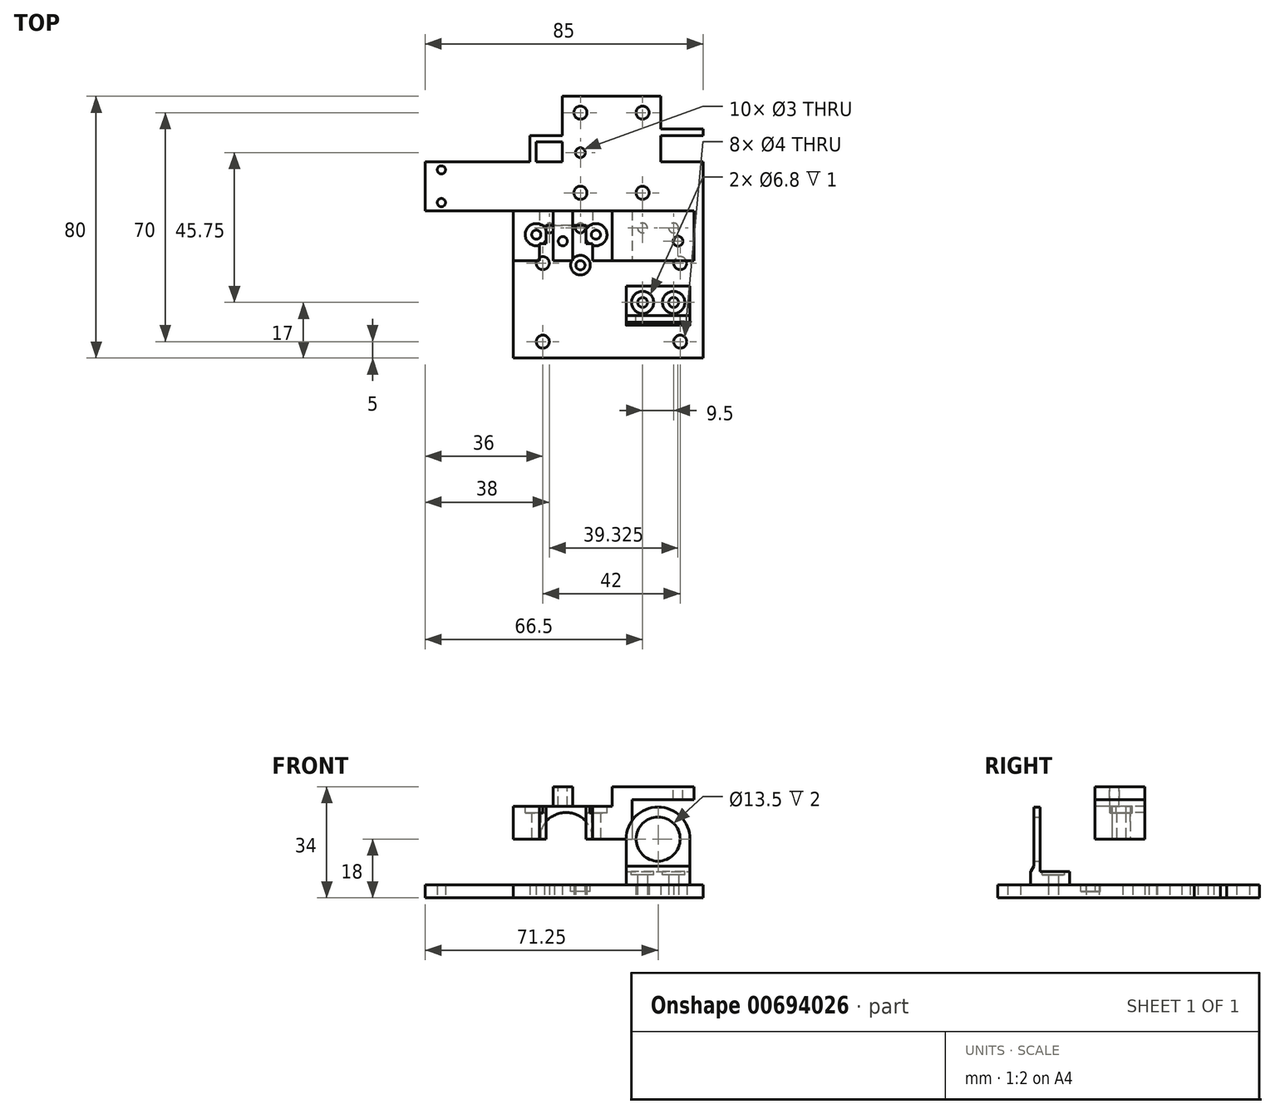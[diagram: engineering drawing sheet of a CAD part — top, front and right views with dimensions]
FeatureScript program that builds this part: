
annotation { "Feature Type Name" : "Feature", "Feature Type Description" : "" }
export const myFeature = defineFeature(function(context is Context, id is Id, definition is map)
    precondition{}
    {
        {
            var Q0;
            Q0=qCreatedBy(makeId("Top.planeOp"),FACE);
            var sketch = newSketch(context, id + "F0", { "sketchPlane" : qUnion([Q0])});
            skLineSegment(sketch, "E0.bottom", {"start": v(0, 0) * mm, "end": v(58, 0) * mm});
            skLineSegment(sketch, "E0.top", {"start": v(0, -60) * mm, "end": v(58, -60) * mm});
            skLineSegment(sketch, "E0.left", {"start": v(0, 0) * mm, "end": v(0, -60) * mm});
            skLineSegment(sketch, "E0.right", {"start": v(58, 0) * mm, "end": v(58, -60) * mm});
            skLineSegment(sketch, "E1.bottom", {"start": v(15, 0) * mm, "end": v(45, 0) * mm});
            skLineSegment(sketch, "E1.top", {"start": v(15, 20) * mm, "end": v(45, 20) * mm});
            skLineSegment(sketch, "E1.left", {"start": v(15, 0) * mm, "end": v(15, 20) * mm});
            skLineSegment(sketch, "E1.right", {"start": v(45, 0) * mm, "end": v(45, 20) * mm});
            skLineSegment(sketch, "E2.bottom", {"start": v(0, 0) * mm, "end": v(-27, 0) * mm});
            skLineSegment(sketch, "E2.top", {"start": v(0, -15) * mm, "end": v(-27, -15) * mm});
            skLineSegment(sketch, "E2.left", {"start": v(0, 0) * mm, "end": v(0, -15) * mm});
            skLineSegment(sketch, "E2.right", {"start": v(-27, 0) * mm, "end": v(-27, -15) * mm});
            skCircle(sketch, "E3", {"center": v(20.5, 15) * mm, "radius": 2 * mm});
            skLineSegment(sketch, "E4", {"start": v(30, 20) * mm, "end": v(30, -60) * mm, "construction": true});
            skCircle(sketch, "E5.MirrorC", {"center": v(39.5, 15) * mm, "radius": 2 * mm});
            skCircle(sketch, "E6", {"center": v(20.5, -9.5) * mm, "radius": 2 * mm});
            skCircle(sketch, "E7.MirrorC", {"center": v(39.5, -9.5) * mm, "radius": 2 * mm});
            skCircle(sketch, "E8", {"center": v(51, -55) * mm, "radius": 2 * mm});
            skCircle(sketch, "E9.MirrorC", {"center": v(9, -55) * mm, "radius": 2 * mm});
            skCircle(sketch, "E10", {"center": v(51, -31) * mm, "radius": 2 * mm});
            skCircle(sketch, "E11.MirrorC", {"center": v(9, -31) * mm, "radius": 2 * mm});
            skCircle(sketch, "E12", {"center": v(-22, -2.5) * mm, "radius": 1.25 * mm});
            skLineSegment(sketch, "E13", {"start": v(-27, -7.5) * mm, "end": v(0, -7.5) * mm, "construction": true});
            skCircle(sketch, "E14.MirrorC", {"center": v(-22, -12.5) * mm, "radius": 1.25 * mm});
            skLineSegment(sketch, "E15", {"start": v(20.5, -9.5) * mm, "end": v(20.5, -31) * mm, "construction": true});
            skCircle(sketch, "E16", {"center": v(20.5, -20.25) * mm, "radius": 1.5 * mm});
            skCircle(sketch, "E17", {"center": v(11, -20.25) * mm, "radius": 1.5 * mm});
            skCircle(sketch, "E18.MirrorC", {"center": v(39.5, -20.25) * mm, "radius": 1.5 * mm});
            skCircle(sketch, "E19.MirrorC", {"center": v(49, -20.25) * mm, "radius": 1.5 * mm});
            skCircle(sketch, "E20", {"center": v(30, -20.25) * mm, "radius": 1.5 * mm});
            skPoint(sketch, "E20.centerSnap0", {"position": v(30, -20) * mm});
            skLineSegment(sketch, "E21", {"start": v(9, -31) * mm, "end": v(9, -55) * mm, "construction": true});
            skLineSegment(sketch, "E22", {"start": v(9, -43) * mm, "end": v(58, -43) * mm, "construction": true});
            skLineSegment(sketch, "E23", {"start": v(39.5, -20.25) * mm, "end": v(39.5, -43) * mm, "construction": true});
            skLineSegment(sketch, "E24", {"start": v(39.5, -31.63) * mm, "end": v(0, -31.63) * mm, "construction": true});
            skCircle(sketch, "E25.MirrorC", {"center": v(49, -43) * mm, "radius": 1.5 * mm});
            skCircle(sketch, "E26.MirrorC", {"center": v(39.5, -43) * mm, "radius": 1.5 * mm});
            skCircle(sketch, "E27", {"center": v(30, -31.63) * mm, "radius": 1.5 * mm});
            skCircle(sketch, "E28", {"center": v(39.5, -31.63) * mm, "radius": 1.5 * mm});
            skCircle(sketch, "E29", {"center": v(20.5, -31.63) * mm, "radius": 1.5 * mm});
            skLineSegment(sketch, "E30", {"start": v(39.5, 15) * mm, "end": v(39.5, -9.5) * mm, "construction": true});
            skCircle(sketch, "E31", {"center": v(39.5, 2.75) * mm, "radius": 1.5 * mm});
            skCircle(sketch, "E32.MirrorC", {"center": v(20.5, 2.75) * mm, "radius": 1.5 * mm});
            skCircle(sketch, "E33", {"center": v(30, 2.75) * mm, "radius": 1.5 * mm});
            skLineSegment(sketch, "E34.bottom", {"start": v(58, 0) * mm, "end": v(45, 0) * mm});
            skLineSegment(sketch, "E34.top", {"start": v(58, 8) * mm, "end": v(45, 8) * mm});
            skLineSegment(sketch, "E34.left", {"start": v(58, 0) * mm, "end": v(58, 8) * mm});
            skLineSegment(sketch, "E34.right", {"start": v(45, 0) * mm, "end": v(45, 8) * mm});
            skLineSegment(sketch, "E35.top", {"start": v(58, 10) * mm, "end": v(45, 10) * mm});
            skLineSegment(sketch, "E35.left", {"start": v(58, 8) * mm, "end": v(58, 10) * mm});
            skLineSegment(sketch, "E35.right", {"start": v(45, 8) * mm, "end": v(45, 10) * mm});
            skLineSegment(sketch, "E36.bottom", {"start": v(58, 8) * mm, "end": v(56, 8) * mm});
            skLineSegment(sketch, "E36.top", {"start": v(58, 0) * mm, "end": v(56, 0) * mm});
            skLineSegment(sketch, "E36.left", {"start": v(58, 8) * mm, "end": v(58, 0) * mm});
            skLineSegment(sketch, "E36.right", {"start": v(56, 8) * mm, "end": v(56, 0) * mm});
            skLineSegment(sketch, "E37.bottom", {"start": v(15, 0) * mm, "end": v(7, 0) * mm});
            skLineSegment(sketch, "E37.top", {"start": v(15, 6) * mm, "end": v(7, 6) * mm});
            skLineSegment(sketch, "E37.left", {"start": v(15, 0) * mm, "end": v(15, 6) * mm});
            skLineSegment(sketch, "E37.right", {"start": v(7, 0) * mm, "end": v(7, 6) * mm});
            skLineSegment(sketch, "E38.0", {"start": v(5, 0) * mm, "end": v(5, 8) * mm});
            skLineSegment(sketch, "E38.1", {"start": v(15, 8) * mm, "end": v(5, 8) * mm});
            skSolve(sketch);
        }
        {
            var Q0;
            Q0=makeQuery(id+"F0.imprint","IMPRINT",FACE,{"disambiguationData":[TD([[makeQuery(id+"F0.imprint","IMPRINT",EDGE,{"derivedFrom":sQuery(id+"F0.wireOp",EDGE,"E0.top")}),1.0]])]});
            var Q1;
            Q1=makeQuery(id+"F0.imprint","IMPRINT",FACE,{"disambiguationData":[TD([[makeQuery(id+"F0.imprint","IMPRINT",EDGE,{"derivedFrom":sQuery(id+"F0.wireOp",EDGE,"E2.bottom")}),1.0]])]});
            var Q2;
            Q2=makeQuery(id+"F0.imprint","IMPRINT",FACE,{"disambiguationData":[TD([[makeQuery(id+"F0.imprint","IMPRINT",EDGE,{"derivedFrom":sQuery(id+"F0.wireOp",EDGE,"E1.bottom")}),1.0]])]});
            var Q3;
            Q3=makeQuery(id+"F0.imprint","IMPRINT",FACE,{"disambiguationData":[TD([[makeQuery(id+"F0.imprint","IMPRINT",EDGE,{"derivedFrom":sQuery(id+"F0.wireOp",EDGE,"E20")}),1.0]])]});
            var Q4;
            Q4=makeQuery(id+"F0.imprint","IMPRINT",FACE,{"disambiguationData":[TD([[makeQuery(id+"F0.imprint","IMPRINT",EDGE,{"derivedFrom":sQuery(id+"F0.wireOp",EDGE,"E18.MirrorC")}),-1.0]])]});
            var Q5;
            Q5=makeQuery(id+"F0.imprint","IMPRINT",FACE,{"disambiguationData":[TD([[makeQuery(id+"F0.imprint","IMPRINT",EDGE,{"derivedFrom":sQuery(id+"F0.wireOp",EDGE,"E19.MirrorC")}),-1.0]])]});
            var Q6;
            Q6=makeQuery(id+"F0.imprint","IMPRINT",FACE,{"disambiguationData":[TD([[makeQuery(id+"F0.imprint","IMPRINT",EDGE,{"derivedFrom":sQuery(id+"F0.wireOp",EDGE,"E27")}),1.0]])]});
            var Q7;
            Q7=makeQuery(id+"F0.imprint","IMPRINT",FACE,{"disambiguationData":[TD([[makeQuery(id+"F0.imprint","IMPRINT",EDGE,{"derivedFrom":sQuery(id+"F0.wireOp",EDGE,"E28")}),1.0]])]});
            var Q8;
            Q8=makeQuery(id+"F0.imprint","IMPRINT",FACE,{"disambiguationData":[TD([[makeQuery(id+"F0.imprint","IMPRINT",EDGE,{"derivedFrom":sQuery(id+"F0.wireOp",EDGE,"E32.MirrorC")}),-1.0]])]});
            var Q9;
            Q9=makeQuery(id+"F0.imprint","IMPRINT",FACE,{"disambiguationData":[TD([[makeQuery(id+"F0.imprint","IMPRINT",EDGE,{"derivedFrom":sQuery(id+"F0.wireOp",EDGE,"E33")}),1.0]])]});
            var Q10;
            Q10=makeQuery(id+"F0.imprint","IMPRINT",FACE,{"disambiguationData":[TD([[makeQuery(id+"F0.imprint","IMPRINT",EDGE,{"derivedFrom":sQuery(id+"F0.wireOp",EDGE,"E31")}),1.0]])]});
            var Q11;
            Q11=makeQuery(id+"F0.imprint","IMPRINT",FACE,{"disambiguationData":[TD([[makeQuery(id+"F0.imprint","IMPRINT",EDGE,{"derivedFrom":sQuery(id+"F0.wireOp",EDGE,"E29")}),1.0]])]});
            var Q12;
            Q12=makeQuery(id+"F0.imprint","IMPRINT",FACE,{"disambiguationData":[TD([[makeQuery(id+"F0.imprint","IMPRINT",EDGE,{"derivedFrom":sQuery(id+"F0.wireOp",EDGE,"E34.top")}),-1.0]])]});
            var Q13;
            Q13=makeQuery(id+"F0.imprint","IMPRINT",FACE,{"disambiguationData":[TD([[makeQuery(id+"F0.imprint","IMPRINT",EDGE,{"derivedFrom":sQuery(id+"F0.wireOp",EDGE,"E36.bottom")}),1.0]])]});
            var Q14;
            {var subQ0=sQuery(id+"F0.wireOp",EDGE,"XzGVJkhi-AcDU-f53J-RqIE-YCnuyh9zdkUA");Q14=makeQuery(id+"F0.imprint","IMPRINT",FACE,{"disambiguationData":[TD([[makeQuery(id+"F0.imprint","IMPRINT",EDGE,{"derivedFrom":subQ0}),-1.0]])]});}
            var Q15;
            Q15 = qSketchRegion(id + "F2", true);
            var Q16;
            {var subQ0=sQuery(id+"F0.wireOp",EDGE,"E37.top");Q16=makeQuery(id+"F0.imprint","IMPRINT",FACE,{"disambiguationData":[TD([[makeQuery(id+"F0.imprint","IMPRINT",EDGE,{"derivedFrom":subQ0}),-1.0]])]});}
            extrude(context, id + "F1", {"entities" : qUnion([Q0, Q1, Q2, Q3, Q4, Q5, Q6, Q7, Q8, Q9, Q10, Q11, Q12, Q13, Q14, Q15, Q16]), "depth" : 4 * mm, "offsetDistance" : 25 * mm});
        }
        {
            var Q0;
            Q0=makeQuery(id+"F1.opExtrude","CAP_FACE",FACE,{"disambiguationData":[OSD([sQuery(id+"F0.wireOp",EDGE,"E0.bottom"),sQuery(id+"F0.wireOp",EDGE,"E0.top"),sQuery(id+"F0.wireOp",EDGE,"E0.left"),sQuery(id+"F0.wireOp",EDGE,"E0.right"),sQuery(id+"F0.wireOp",EDGE,"E1.top"),sQuery(id+"F0.wireOp",EDGE,"E1.left"),sQuery(id+"F0.wireOp",EDGE,"E1.right"),sQuery(id+"F0.wireOp",EDGE,"E2.bottom"),sQuery(id+"F0.wireOp",EDGE,"E2.top"),sQuery(id+"F0.wireOp",EDGE,"E2.right"),sQuery(id+"F0.wireOp",EDGE,"E3"),sQuery(id+"F0.wireOp",EDGE,"E5.MirrorC"),sQuery(id+"F0.wireOp",EDGE,"E6"),sQuery(id+"F0.wireOp",EDGE,"E7.MirrorC"),sQuery(id+"F0.wireOp",EDGE,"E8"),sQuery(id+"F0.wireOp",EDGE,"E9.MirrorC"),sQuery(id+"F0.wireOp",EDGE,"E10"),sQuery(id+"F0.wireOp",EDGE,"E11.MirrorC"),sQuery(id+"F0.wireOp",EDGE,"E12"),sQuery(id+"F0.wireOp",EDGE,"E14.MirrorC"),sQuery(id+"F0.wireOp",EDGE,"E16"),sQuery(id+"F0.wireOp",EDGE,"E17"),sQuery(id+"F0.wireOp",EDGE,"E18.MirrorC"),sQuery(id+"F0.wireOp",EDGE,"E19.MirrorC"),sQuery(id+"F0.wireOp",EDGE,"E20"),sQuery(id+"F0.wireOp",EDGE,"E25.MirrorC"),sQuery(id+"F0.wireOp",EDGE,"E26.MirrorC"),sQuery(id+"F0.wireOp",EDGE,"a45dcdff-8f47-47a6-94de-daccb21566b90.MirrorC"),sQuery(id+"F0.wireOp",EDGE,"c506a873-8e33-4dee-948d-999e04e901bd0.MirrorC"),sQuery(id+"F0.wireOp",EDGE,"0d328794-d52e-4739-910c-511e7e9b0b190.MirrorC"),sQuery(id+"F0.wireOp",EDGE,"E27"),sQuery(id+"F0.wireOp",EDGE,"E28"),sQuery(id+"F0.wireOp",EDGE,"E29"),sQuery(id+"F0.wireOp",EDGE,"E31"),sQuery(id+"F0.wireOp",EDGE,"E32.MirrorC"),sQuery(id+"F0.wireOp",EDGE,"E33")])],"isStart":false});
            var sketch = newSketch(context, id + "F2", { "sketchPlane" : qUnion([Q0])});
            skLineSegment(sketch, "E39.0", {"start": v(0, -15) * mm, "end": v(0, -60) * mm});
            skLineSegment(sketch, "E39.1", {"start": v(-27, 0) * mm, "end": v(5, 0) * mm});
            skLineSegment(sketch, "E39.2", {"start": v(0, -15) * mm, "end": v(-27, -15) * mm});
            skLineSegment(sketch, "E39.3", {"start": v(0, -60) * mm, "end": v(58, -60) * mm});
            skLineSegment(sketch, "E39.4", {"start": v(58, -60) * mm, "end": v(58, -60) * mm});
            skLineSegment(sketch, "E39.5", {"start": v(5, 0) * mm, "end": v(58, 0) * mm});
            skLineSegment(sketch, "E39.6", {"start": v(45, 0) * mm, "end": v(45, 20) * mm});
            skLineSegment(sketch, "E39.7", {"start": v(15, 0) * mm, "end": v(15, 20) * mm});
            skLineSegment(sketch, "E39.8", {"start": v(15, 20) * mm, "end": v(45, 20) * mm});
            skCircle(sketch, "E39.9", {"center": v(11, -20.25) * mm, "radius": 1.5 * mm});
            skCircle(sketch, "E39.10", {"center": v(20.5, -20.25) * mm, "radius": 1.5 * mm});
            skCircle(sketch, "E39.11", {"center": v(20.5, -31.63) * mm, "radius": 1.4 * mm});
            skCircle(sketch, "E40.0", {"center": v(9, -31) * mm, "radius": 2 * mm});
            skLineSegment(sketch, "E41", {"start": v(7, 0) * mm, "end": v(7, -60) * mm, "construction": true});
            skCircle(sketch, "E42.0", {"center": v(20.5, -9.5) * mm, "radius": 2 * mm});
            skLineSegment(sketch, "E43", {"start": v(20.5, -9.5) * mm, "end": v(20.5, -20.25) * mm, "construction": true});
            skPoint(sketch, "E44", {"position": v(20.5, -14.88) * mm});
            skLineSegment(sketch, "E45", {"start": v(7, -15) * mm, "end": v(25.25, -15) * mm});
            skLineSegment(sketch, "E46", {"start": v(7, -37.31) * mm, "end": v(25.25, -37.31) * mm});
            skLineSegment(sketch, "E47", {"start": v(25.25, -37.31) * mm, "end": v(25.25, -15) * mm});
            skCircle(sketch, "E48", {"center": v(9, -31) * mm, "radius": 6.31 * mm});
            skLineSegment(sketch, "E49", {"start": v(9, -24.69) * mm, "end": v(7, -24.69) * mm});
            skLineSegment(sketch, "E50", {"start": v(15.31, -31) * mm, "end": v(15.31, -37.31) * mm});
            skLineSegment(sketch, "E51", {"start": v(7, -15) * mm, "end": v(7, -24.69) * mm});
            skSolve(sketch);
        }
        {
            var Q0;
            Q0=makeQuery(id+"F2.imprint","IMPRINT",FACE,{"disambiguationData":[TD([[makeQuery(id+"F2.imprint","IMPRINT",EDGE,{"derivedFrom":sQuery(id+"F2.wireOp",EDGE,"E39.9")}),-1.0]])]});
            extrude(context, id + "F3", {"entities" : qUnion([Q0]), "depth" : 4 * mm, "offsetDistance" : 25 * mm});
        }
        {
            var Q0;
            Q0=makeQuery(id+"F1.opExtrude","CAP_FACE",FACE,{"disambiguationData":[OSD([sQuery(id+"F0.wireOp",EDGE,"E0.bottom"),sQuery(id+"F0.wireOp",EDGE,"E0.top"),sQuery(id+"F0.wireOp",EDGE,"E0.left"),sQuery(id+"F0.wireOp",EDGE,"E0.right"),sQuery(id+"F0.wireOp",EDGE,"E1.top"),sQuery(id+"F0.wireOp",EDGE,"E1.left"),sQuery(id+"F0.wireOp",EDGE,"E1.right"),sQuery(id+"F0.wireOp",EDGE,"E2.bottom"),sQuery(id+"F0.wireOp",EDGE,"E2.top"),sQuery(id+"F0.wireOp",EDGE,"E2.right"),sQuery(id+"F0.wireOp",EDGE,"E3"),sQuery(id+"F0.wireOp",EDGE,"E5.MirrorC"),sQuery(id+"F0.wireOp",EDGE,"E6"),sQuery(id+"F0.wireOp",EDGE,"E7.MirrorC"),sQuery(id+"F0.wireOp",EDGE,"E8"),sQuery(id+"F0.wireOp",EDGE,"E9.MirrorC"),sQuery(id+"F0.wireOp",EDGE,"E10"),sQuery(id+"F0.wireOp",EDGE,"E11.MirrorC"),sQuery(id+"F0.wireOp",EDGE,"E12"),sQuery(id+"F0.wireOp",EDGE,"E14.MirrorC"),sQuery(id+"F0.wireOp",EDGE,"E16"),sQuery(id+"F0.wireOp",EDGE,"E17"),sQuery(id+"F0.wireOp",EDGE,"E25.MirrorC"),sQuery(id+"F0.wireOp",EDGE,"E26.MirrorC")])],"isStart":false});
            var sketch = newSketch(context, id + "F4", { "sketchPlane" : qUnion([Q0])});
            skCircle(sketch, "E52.0", {"center": v(11, -20.25) * mm, "radius": 1.5 * mm});
            skCircle(sketch, "E52.1", {"center": v(20.5, -20.25) * mm, "radius": 1.5 * mm});
            skCircle(sketch, "E52.2", {"center": v(20.5, -31.63) * mm, "radius": 1.4 * mm});
            skCircle(sketch, "E53", {"center": v(20.5, -31.63) * mm, "radius": 3 * mm});
            skLineSegment(sketch, "E54.0", {"start": v(7, -15) * mm, "end": v(25.25, -15) * mm});
            skLineSegment(sketch, "E54.1", {"start": v(7, -15) * mm, "end": v(7, -24.69) * mm});
            skLineSegment(sketch, "E54.4", {"start": v(25.25, -37.31) * mm, "end": v(25.25, -15) * mm});
            skLineSegment(sketch, "E54.5", {"start": v(9, -24.69) * mm, "end": v(7, -24.69) * mm});
            skArc(sketch, "E54.6", {"start": v(15.31, -31) * mm, "mid": v(13.46, -26.54) * mm, "end": v(9, -24.69) * mm});
            skLineSegment(sketch, "E54.7", {"start": v(15.31, -31) * mm, "end": v(15.31, -37.31) * mm});
            skLineSegment(sketch, "E54.8", {"start": v(15.31, -37.31) * mm, "end": v(25.25, -37.31) * mm});
            skLineSegment(sketch, "E55", {"start": v(9, -24.69) * mm, "end": v(25.25, -24.69) * mm});
            skSolve(sketch);
        }
        {
            var Q0;
            Q0=makeQuery(id+"F4.imprint","IMPRINT",FACE,{"disambiguationData":[TD([[makeQuery(id+"F4.imprint","IMPRINT",EDGE,{"derivedFrom":sQuery(id+"F4.wireOp",EDGE,"E52.2")}),-1.0]])]});
            extrude(context, id + "F5", {"entities" : qUnion([Q0]), "operationType" : NewBodyOperationType.REMOVE, "oppositeDirection" : true, "depth" : 2 * mm, "offsetDistance" : 25 * mm});
        }
        {
            var Q0;
            Q0=makeQuery(id+"F4.imprint","IMPRINT",FACE,{"disambiguationData":[TD([[makeQuery(id+"F4.imprint","IMPRINT",EDGE,{"derivedFrom":sQuery(id+"F4.wireOp",EDGE,"E52.0")}),-1.0]])]});
            extrude(context, id + "F6", {"entities" : qUnion([Q0]), "depth" : 4 * mm, "offsetDistance" : 25 * mm});
        }
        {
            var Q0;
            Q0=makeQuery(id+"F6.opExtrude","CAP_FACE",FACE,{"disambiguationData":[OSD([sQuery(id+"F4.wireOp",EDGE,"E52.0"),sQuery(id+"F4.wireOp",EDGE,"E52.1"),sQuery(id+"F4.wireOp",EDGE,"E54.0"),sQuery(id+"F4.wireOp",EDGE,"E54.1"),sQuery(id+"F4.wireOp",EDGE,"E54.4"),sQuery(id+"F4.wireOp",EDGE,"E54.5"),sQuery(id+"F4.wireOp",EDGE,"E55")])],"isStart":false});
            var sketch = newSketch(context, id + "F7", { "sketchPlane" : qUnion([Q0])});
            skLineSegment(sketch, "E56.0", {"start": v(7, -15) * mm, "end": v(7, -24.69) * mm});
            skLineSegment(sketch, "E56.1", {"start": v(7, -15) * mm, "end": v(25.25, -15) * mm});
            skLineSegment(sketch, "E56.2", {"start": v(25.25, -24.69) * mm, "end": v(7, -24.69) * mm});
            skLineSegment(sketch, "E56.3", {"start": v(25.25, -24.69) * mm, "end": v(25.25, -15) * mm});
            skLineSegment(sketch, "E57.0", {"start": v(15.31, -31) * mm, "end": v(15.31, -37.31) * mm});
            skLineSegment(sketch, "E57.1", {"start": v(15.31, -37.31) * mm, "end": v(25.25, -37.31) * mm});
            skLineSegment(sketch, "E57.2", {"start": v(25.25, -37.31) * mm, "end": v(25.25, -15) * mm});
            skArc(sketch, "E57.3", {"start": v(15.31, -31) * mm, "mid": v(13.46, -26.54) * mm, "end": v(9, -24.69) * mm});
            skLineSegment(sketch, "E58", {"start": v(7, -24.69) * mm, "end": v(7, -37.31) * mm});
            skLineSegment(sketch, "E59", {"start": v(7, -37.31) * mm, "end": v(15.31, -37.31) * mm});
            skLineSegment(sketch, "E60.bottom", {"start": v(7, -15) * mm, "end": v(4, -15) * mm});
            skLineSegment(sketch, "E60.top", {"start": v(7, -37.31) * mm, "end": v(4, -37.31) * mm});
            skLineSegment(sketch, "E60.left", {"start": v(7, -15) * mm, "end": v(7, -37.31) * mm});
            skLineSegment(sketch, "E60.right", {"start": v(4, -15) * mm, "end": v(4, -37.31) * mm});
            skLineSegment(sketch, "E61.bottom", {"start": v(25.25, -15) * mm, "end": v(28.25, -15) * mm});
            skLineSegment(sketch, "E61.top", {"start": v(25.25, -37.31) * mm, "end": v(28.25, -37.31) * mm});
            skLineSegment(sketch, "E61.left", {"start": v(25.25, -15) * mm, "end": v(25.25, -37.31) * mm});
            skLineSegment(sketch, "E61.right", {"start": v(28.25, -15) * mm, "end": v(28.25, -37.31) * mm});
            skSolve(sketch);
        }
        {
            var Q0;
            {var subQ1=sQuery(id+"F7.wireOp",EDGE,"E56.1");Q0=makeQuery(id+"F7.imprint","IMPRINT",FACE,{"disambiguationData":[TD([[makeQuery(id+"F7.imprint","IMPRINT",EDGE,{"derivedFrom":subQ1}),-1.0]])]});}
            var Q1;
            {var subQ3=sQuery(id+"F7.wireOp",EDGE,"E60.bottom");Q1=makeQuery(id+"F7.imprint","IMPRINT",FACE,{"disambiguationData":[TD([[makeQuery(id+"F7.imprint","IMPRINT",EDGE,{"derivedFrom":subQ3}),1.0]])]});}
            var Q2;
            Q2=makeQuery(id+"F7.imprint","IMPRINT",FACE,{"disambiguationData":[TD([[makeQuery(id+"F7.imprint","IMPRINT",EDGE,{"derivedFrom":sQuery(id+"F7.wireOp",EDGE,"E57.0")}),-1.0]])]});
            var Q3;
            Q3=makeQuery(id+"F7.imprint","IMPRINT",FACE,{"disambiguationData":[TD([[makeQuery(id+"F7.imprint","IMPRINT",EDGE,{"derivedFrom":sQuery(id+"F7.wireOp",EDGE,"E57.0")}),1.0]])]});
            var Q4;
            {var subQ1=sQuery(id+"F7.wireOp",EDGE,"E61.bottom");Q4=makeQuery(id+"F7.imprint","IMPRINT",FACE,{"disambiguationData":[TD([[makeQuery(id+"F7.imprint","IMPRINT",EDGE,{"derivedFrom":subQ1}),-1.0]])]});}
            var Q5;
            Q5=makeQuery(id+"F7.imprint","IMPRINT",FACE,{"disambiguationData":[TD([[makeQuery(id+"F7.imprint","IMPRINT",EDGE,{"derivedFrom":makeQuery(id+"F6.opExtrude","CAP_EDGE",EDGE,{"disambiguationData":[OSD([sQuery(id+"F4.wireOp",EDGE,"E52.0")])],"isStart":false})}),1.0]])]});
            var Q6;
            Q6=makeQuery(id+"F7.imprint","IMPRINT",FACE,{"disambiguationData":[TD([[makeQuery(id+"F7.imprint","IMPRINT",EDGE,{"derivedFrom":makeQuery(id+"F6.opExtrude","CAP_EDGE",EDGE,{"disambiguationData":[OSD([sQuery(id+"F4.wireOp",EDGE,"E52.1")])],"isStart":false})}),1.0]])]});
            extrude(context, id + "F8", {"entities" : qUnion([Q0, Q1, Q2, Q3, Q4, Q5, Q6]), "operationType" : NewBodyOperationType.ADD, "depth" : 10 * mm, "offsetDistance" : 25 * mm});
        }
        {
            var Q0;
            Q0=makeQuery(id+"F8.opExtrude","CAP_FACE",FACE,{"disambiguationData":[OSD([sQuery(id+"F7.wireOp",EDGE,"E56.0"),sQuery(id+"F7.wireOp",EDGE,"E56.1"),sQuery(id+"F7.wireOp",EDGE,"E57.1"),sQuery(id+"F7.wireOp",EDGE,"E57.2"),sQuery(id+"F7.wireOp",EDGE,"E58"),sQuery(id+"F7.wireOp",EDGE,"E59")])],"isStart":false});
            var sketch = newSketch(context, id + "F9", { "sketchPlane" : qUnion([Q0])});
            skLineSegment(sketch, "E62", {"start": v(16.13, -15) * mm, "end": v(16.13, -37.31) * mm, "construction": true});
            skLineSegment(sketch, "E63.bottom", {"start": v(16.13, -15) * mm, "end": v(24.23, -15) * mm});
            skLineSegment(sketch, "E63.top", {"start": v(16.13, -19.5) * mm, "end": v(24.23, -19.5) * mm});
            skLineSegment(sketch, "E63.left", {"start": v(16.13, -15) * mm, "end": v(16.13, -19.5) * mm});
            skLineSegment(sketch, "E63.right", {"start": v(24.23, -15) * mm, "end": v(24.23, -19.5) * mm});
            skLineSegment(sketch, "E64.bottom", {"start": v(16.13, -19.5) * mm, "end": v(22.23, -19.5) * mm});
            skLineSegment(sketch, "E64.top", {"start": v(16.13, -25.1) * mm, "end": v(22.23, -25.1) * mm});
            skLineSegment(sketch, "E64.left", {"start": v(16.13, -19.5) * mm, "end": v(16.13, -25.1) * mm});
            skLineSegment(sketch, "E64.right", {"start": v(22.23, -19.5) * mm, "end": v(22.23, -25.1) * mm});
            skLineSegment(sketch, "E65.bottom", {"start": v(16.13, -25.1) * mm, "end": v(24.23, -25.1) * mm});
            skLineSegment(sketch, "E65.top", {"start": v(16.13, -30.3) * mm, "end": v(24.23, -30.3) * mm});
            skLineSegment(sketch, "E65.left", {"start": v(16.13, -25.1) * mm, "end": v(16.13, -30.3) * mm});
            skLineSegment(sketch, "E65.right", {"start": v(24.23, -25.1) * mm, "end": v(24.23, -30.3) * mm});
            skLineSegment(sketch, "E66.left", {"start": v(16.13, -30.3) * mm, "end": v(16.13, -37.31) * mm});
            skLineSegment(sketch, "E67", {"start": v(22.23, -22.3) * mm, "end": v(28.25, -22.3) * mm, "construction": true});
            skCircle(sketch, "E68", {"center": v(25.24, -22.3) * mm, "radius": 1.4 * mm});
            skCircle(sketch, "E69.MirrorC", {"center": v(7.01, -22.3) * mm, "radius": 1.4 * mm});
            skSolve(sketch);
        }
        {
            var Q0;
            Q0=makeQuery(id+"F9.imprint","IMPRINT",FACE,{"disambiguationData":[TD([[makeQuery(id+"F9.imprint","IMPRINT",EDGE,{"derivedFrom":sQuery(id+"F9.wireOp",EDGE,"E65.top")}),1.0]])]});
            var Q1;
            {var subQ1=sQuery(id+"F9.wireOp",EDGE,"E65.left");Q1=makeQuery(id+"F9.imprint","IMPRINT",FACE,{"disambiguationData":[TD([[makeQuery(id+"F9.imprint","IMPRINT",EDGE,{"derivedFrom":subQ1}),1.0]])]});}
            var Q2;
            Q2=makeQuery(id+"F9.imprint","IMPRINT",FACE,{"disambiguationData":[TD([[makeQuery(id+"F9.imprint","IMPRINT",EDGE,{"derivedFrom":sQuery(id+"F9.wireOp",EDGE,"E63.bottom")}),-1.0]])]});
            var Q3;
            Q3=makeQuery(id+"F9.imprint","IMPRINT",FACE,{"disambiguationData":[TD([[makeQuery(id+"F9.imprint","IMPRINT",EDGE,{"derivedFrom":sQuery(id+"F9.wireOp",EDGE,"E64.bottom")}),-1.0]])]});
            var Q4;
            Q4=sQuery(id+"F9.wireOp",EDGE,"E64.left");
            revolve(context, id + "F10", {"operationType" : NewBodyOperationType.REMOVE, "entities" : qUnion([Q0, Q1, Q2, Q3]), "axis" : qUnion([Q4]), "revolveType" : RevolveType.FULL, "oppositeDirection" : true});
        }
        {
            var Q0;
            Q0=makeQuery(id+"F8.opExtrude","CAP_FACE",FACE,{"disambiguationData":[OSD([sQuery(id+"F7.wireOp",EDGE,"E56.0"),sQuery(id+"F7.wireOp",EDGE,"E56.1"),sQuery(id+"F7.wireOp",EDGE,"E57.1"),sQuery(id+"F7.wireOp",EDGE,"E57.2"),sQuery(id+"F7.wireOp",EDGE,"E58"),sQuery(id+"F7.wireOp",EDGE,"E59")])],"isStart":false});
            var sketch = newSketch(context, id + "F11", { "sketchPlane" : qUnion([Q0])});
            skLineSegment(sketch, "E70.bottom", {"start": v(4, -30.3) * mm, "end": v(28.25, -30.3) * mm});
            skLineSegment(sketch, "E70.top", {"start": v(4, -37.31) * mm, "end": v(28.25, -37.31) * mm});
            skLineSegment(sketch, "E70.left", {"start": v(4, -30.3) * mm, "end": v(4, -37.31) * mm});
            skLineSegment(sketch, "E70.right", {"start": v(28.25, -30.3) * mm, "end": v(28.25, -37.31) * mm});
            skSolve(sketch);
        }
        {
            var Q0;
            Q0=makeQuery(id+"F11.imprint","IMPRINT",FACE,{"disambiguationData":[TD([[makeQuery(id+"F11.imprint","IMPRINT",EDGE,{"derivedFrom":sQuery(id+"F11.wireOp",EDGE,"E70.top")}),-1.0]])]});
            extrude(context, id + "F12", {"entities" : qUnion([Q0]), "operationType" : NewBodyOperationType.REMOVE, "endBound" : BoundingType.UP_TO_NEXT, "oppositeDirection" : true, "depth" : 25 * mm, "offsetDistance" : 25 * mm});
        }
        {
            var Q0;
            {var subQ0=sQuery(id+"F7.wireOp",EDGE,"E60.right");var subQ1=sQuery(id+"F7.wireOp",EDGE,"E61.bottom");var subQ2=sQuery(id+"F7.wireOp",EDGE,"E60.bottom");var subQ3=sQuery(id+"F7.wireOp",EDGE,"E56.1");Q0=makeQuery(id+"F12.boolean.opBoolean","SPLIT",FACE,{"disambiguationData":[TD([makeQuery(id+"F8.opExtrude","SWEPT_FACE",FACE,{"disambiguationData":[OSD([subQ0])]})])],"derivedFrom":makeQuery(id+"F8.opExtrude","CAP_FACE",FACE,{"disambiguationData":[OSD([subQ3,sQuery(id+"F7.wireOp",EDGE,"E57.1"),sQuery(id+"F7.wireOp",EDGE,"E59"),subQ2,sQuery(id+"F7.wireOp",EDGE,"E60.top"),subQ0,subQ1,sQuery(id+"F7.wireOp",EDGE,"E61.top"),sQuery(id+"F7.wireOp",EDGE,"E61.right")])],"isStart":false})});}
            var sketch = newSketch(context, id + "F13", { "sketchPlane" : qUnion([Q0])});
            skLineSegment(sketch, "E71.0", {"start": v(8.03, -19.5) * mm, "end": v(8.03, -15) * mm});
            skLineSegment(sketch, "E71.1", {"start": v(4, -15) * mm, "end": v(8.03, -15) * mm});
            skLineSegment(sketch, "E71.2", {"start": v(4, -15) * mm, "end": v(4, -30.3) * mm});
            skLineSegment(sketch, "E71.3", {"start": v(10.03, -25.1) * mm, "end": v(10.03, -19.5) * mm});
            skLineSegment(sketch, "E71.4", {"start": v(8.03, -19.5) * mm, "end": v(10.03, -19.5) * mm});
            skLineSegment(sketch, "E71.5", {"start": v(8.03, -25.1) * mm, "end": v(10.03, -25.1) * mm});
            skLineSegment(sketch, "E71.6", {"start": v(8.03, -30.3) * mm, "end": v(8.03, -25.1) * mm});
            skLineSegment(sketch, "E71.7", {"start": v(4, -30.3) * mm, "end": v(8.03, -30.3) * mm});
            skLineSegment(sketch, "E71.8", {"start": v(24.23, -30.3) * mm, "end": v(28.25, -30.3) * mm});
            skLineSegment(sketch, "E71.9", {"start": v(24.23, -25.1) * mm, "end": v(24.23, -30.3) * mm});
            skLineSegment(sketch, "E71.10", {"start": v(22.23, -19.5) * mm, "end": v(22.23, -25.1) * mm});
            skLineSegment(sketch, "E71.11", {"start": v(22.23, -25.1) * mm, "end": v(24.23, -25.1) * mm});
            skLineSegment(sketch, "E71.12", {"start": v(22.23, -19.5) * mm, "end": v(24.23, -19.5) * mm});
            skLineSegment(sketch, "E71.13", {"start": v(24.23, -15) * mm, "end": v(24.23, -19.5) * mm});
            skLineSegment(sketch, "E71.14", {"start": v(24.23, -15) * mm, "end": v(28.25, -15) * mm});
            skLineSegment(sketch, "E71.15", {"start": v(28.25, -15) * mm, "end": v(28.25, -30.3) * mm});
            skLineSegment(sketch, "E72", {"start": v(10.03, -22.3) * mm, "end": v(4, -22.3) * mm, "construction": true});
            skPoint(sketch, "E72.endSnap0", {"position": v(4, -22.65) * mm});
            skLineSegment(sketch, "E73", {"start": v(22.23, -22.3) * mm, "end": v(28.25, -22.3) * mm, "construction": true});
            skPoint(sketch, "E73.endSnap0", {"position": v(28.25, -22.65) * mm});
            skCircle(sketch, "E74", {"center": v(7.01, -22.3) * mm, "radius": 1.4 * mm});
            skCircle(sketch, "E75", {"center": v(25.24, -22.3) * mm, "radius": 1.4 * mm});
            skSolve(sketch);
        }
        {
            var Q0;
            Q0=makeQuery(id+"F13.imprint","IMPRINT",FACE,{"disambiguationData":[TD([[makeQuery(id+"F13.imprint","IMPRINT",EDGE,{"derivedFrom":sQuery(id+"F13.wireOp",EDGE,"E74")}),1.0]])]});
            var Q1;
            Q1=makeQuery(id+"F13.imprint","IMPRINT",FACE,{"disambiguationData":[TD([[makeQuery(id+"F13.imprint","IMPRINT",EDGE,{"derivedFrom":sQuery(id+"F13.wireOp",EDGE,"E75")}),1.0]])]});
            var Q2;
            {var subQ0=sQuery(id+"F7.wireOp",EDGE,"E61.right");var subQ1=sQuery(id+"F7.wireOp",EDGE,"E60.right");var subQ2=sQuery(id+"F7.wireOp",EDGE,"E61.top");var subQ3=sQuery(id+"F7.wireOp",EDGE,"E60.top");var subQ4=sQuery(id+"F7.wireOp",EDGE,"E59");var subQ5=sQuery(id+"F7.wireOp",EDGE,"E57.1");var subQ6=sQuery(id+"F7.wireOp",EDGE,"E61.bottom");var subQ7=sQuery(id+"F7.wireOp",EDGE,"E60.bottom");var subQ8=sQuery(id+"F7.wireOp",EDGE,"E56.1");Q2=makeQuery(id+"F8.boolean.opBoolean","SPLIT",FACE,{"disambiguationData":[TD([makeQuery(id+"F6.opExtrude","SWEPT_FACE",FACE,{"disambiguationData":[OSD([sQuery(id+"F4.wireOp",EDGE,"E54.0")])]})])],"derivedFrom":makeQuery(id+"F8.opExtrude","CAP_FACE",FACE,{"disambiguationData":[OSD([subQ8,subQ5,subQ4,subQ7,subQ3,subQ1,subQ6,subQ2,subQ0])],"isStart":true})});}
            extrude(context, id + "F14", {"entities" : qUnion([Q0, Q1]), "operationType" : NewBodyOperationType.REMOVE, "oppositeDirection" : true, "depth" : 6 * mm, "endBoundEntityFace" : qUnion([Q2]), "offsetDistance" : 25 * mm});
        }
        {
            var Q0;
            {var subQ0=sQuery(id+"F7.wireOp",EDGE,"E60.right");var subQ1=sQuery(id+"F7.wireOp",EDGE,"E61.bottom");var subQ2=sQuery(id+"F7.wireOp",EDGE,"E60.bottom");var subQ3=sQuery(id+"F7.wireOp",EDGE,"E56.1");Q0=makeQuery(id+"F12.boolean.opBoolean","SPLIT",FACE,{"disambiguationData":[TD([makeQuery(id+"F8.opExtrude","SWEPT_FACE",FACE,{"disambiguationData":[OSD([subQ0])]})])],"derivedFrom":makeQuery(id+"F8.opExtrude","CAP_FACE",FACE,{"disambiguationData":[OSD([subQ3,sQuery(id+"F7.wireOp",EDGE,"E57.1"),sQuery(id+"F7.wireOp",EDGE,"E59"),subQ2,sQuery(id+"F7.wireOp",EDGE,"E60.top"),subQ0,subQ1,sQuery(id+"F7.wireOp",EDGE,"E61.top"),sQuery(id+"F7.wireOp",EDGE,"E61.right")])],"isStart":false})});}
            var sketch = newSketch(context, id + "F15", { "sketchPlane" : qUnion([Q0])});
            skLineSegment(sketch, "E76.0", {"start": v(4, -15) * mm, "end": v(8.03, -15) * mm});
            skLineSegment(sketch, "E76.1", {"start": v(24.23, -15) * mm, "end": v(28.25, -15) * mm});
            skLineSegment(sketch, "E76.2", {"start": v(28.25, -15) * mm, "end": v(28.25, -30.3) * mm});
            skLineSegment(sketch, "E76.3", {"start": v(24.23, -30.3) * mm, "end": v(28.25, -30.3) * mm});
            skLineSegment(sketch, "E76.4", {"start": v(4, -30.3) * mm, "end": v(8.03, -30.3) * mm});
            skLineSegment(sketch, "E76.5", {"start": v(4, -15) * mm, "end": v(4, -30.3) * mm});
            skLineSegment(sketch, "E76.6", {"start": v(8.03, -19.5) * mm, "end": v(8.03, -15) * mm});
            skLineSegment(sketch, "E76.7", {"start": v(10.03, -25.1) * mm, "end": v(10.03, -19.5) * mm});
            skLineSegment(sketch, "E76.8", {"start": v(8.03, -25.1) * mm, "end": v(10.03, -25.1) * mm});
            skLineSegment(sketch, "E76.9", {"start": v(8.03, -30.3) * mm, "end": v(8.03, -25.1) * mm});
            skLineSegment(sketch, "E76.10", {"start": v(22.23, -19.5) * mm, "end": v(22.23, -25.1) * mm});
            skLineSegment(sketch, "E76.11", {"start": v(22.23, -19.5) * mm, "end": v(24.23, -19.5) * mm});
            skLineSegment(sketch, "E76.12", {"start": v(24.23, -15) * mm, "end": v(24.23, -19.5) * mm});
            skCircle(sketch, "E76.13", {"center": v(7.01, -22.3) * mm, "radius": 1.4 * mm});
            skCircle(sketch, "E76.14", {"center": v(25.24, -22.3) * mm, "radius": 1.4 * mm});
            skLineSegment(sketch, "E76.15", {"start": v(22.23, -25.1) * mm, "end": v(24.23, -25.1) * mm});
            skLineSegment(sketch, "E76.16", {"start": v(24.23, -25.1) * mm, "end": v(24.23, -30.3) * mm});
            skLineSegment(sketch, "E76.17", {"start": v(7, -15) * mm, "end": v(25.25, -15) * mm});
            skLineSegment(sketch, "E76.18", {"start": v(28.25, -30.3) * mm, "end": v(4, -30.3) * mm});
            skLineSegment(sketch, "E77.bottom", {"start": v(4, -15) * mm, "end": v(28.25, -15) * mm});
            skLineSegment(sketch, "E77.top", {"start": v(4, -30.3) * mm, "end": v(28.25, -30.3) * mm});
            skLineSegment(sketch, "E78.bottom", {"start": v(4, -15) * mm, "end": v(0, -15) * mm});
            skLineSegment(sketch, "E78.top", {"start": v(4, -30.3) * mm, "end": v(0, -30.3) * mm});
            skLineSegment(sketch, "E78.right", {"start": v(0, -15) * mm, "end": v(0, -30.3) * mm});
            skLineSegment(sketch, "E79.bottom", {"start": v(28.25, -15) * mm, "end": v(32.25, -15) * mm});
            skLineSegment(sketch, "E79.top", {"start": v(28.25, -30.3) * mm, "end": v(32.25, -30.3) * mm});
            skLineSegment(sketch, "E79.right", {"start": v(32.25, -15) * mm, "end": v(32.25, -30.3) * mm});
            skSolve(sketch);
        }
        {
            var Q0;
            Q0=makeQuery(id+"F15.imprint","IMPRINT",FACE,{"disambiguationData":[TD([[makeQuery(id+"F15.imprint","IMPRINT",EDGE,{"derivedFrom":sQuery(id+"F15.wireOp",EDGE,"E76.10")}),1.0]])]});
            var Q1;
            {var subQ3=sQuery(id+"F15.wireOp",EDGE,"E76.6");Q1=makeQuery(id+"F15.imprint","IMPRINT",FACE,{"disambiguationData":[TD([[makeQuery(id+"F15.imprint","IMPRINT",EDGE,{"derivedFrom":subQ3}),1.0]])]});}
            var Q2;
            Q2=makeQuery(id+"F15.imprint","IMPRINT",FACE,{"disambiguationData":[TD([[makeQuery(id+"F15.imprint","IMPRINT",EDGE,{"derivedFrom":sQuery(id+"F15.wireOp",EDGE,"9Krwsxpj-zdF2-yljV-SxoK-9TikhDzbr8sP.bottom")}),-1.0]])]});
            var Q3;
            Q3=makeQuery(id+"F15.imprint","IMPRINT",FACE,{"disambiguationData":[TD([[makeQuery(id+"F15.imprint","IMPRINT",EDGE,{"derivedFrom":sQuery(id+"F15.wireOp",EDGE,"GVNCQcvD-eED8-fHpM-u7qk-yg8l6uwgyDDk.bottom")}),1.0]])]});
            var Q4;
            Q4=makeQuery(id+"F15.imprint","IMPRINT",FACE,{"disambiguationData":[TD([[makeQuery(id+"F15.imprint","IMPRINT",EDGE,{"derivedFrom":sQuery(id+"F15.wireOp",EDGE,"9Krwsxpj-zdF2-yljV-SxoK-9TikhDzbr8sP.top")}),1.0]])]});
            var Q5;
            Q5=makeQuery(id+"F15.imprint","IMPRINT",FACE,{"disambiguationData":[TD([[makeQuery(id+"F15.imprint","IMPRINT",EDGE,{"derivedFrom":sQuery(id+"F15.wireOp",EDGE,"pLIxteJy-nw9s-1QCV-hGO4-gRVc7qcWzNH9.top")}),-1.0]])]});
            var Q6;
            Q6=makeQuery(id+"F15.imprint","IMPRINT",FACE,{"disambiguationData":[TD([[makeQuery(id+"F15.imprint","IMPRINT",EDGE,{"derivedFrom":sQuery(id+"F15.wireOp",EDGE,"GVNCQcvD-eED8-fHpM-u7qk-yg8l6uwgyDDk.top")}),-1.0]])]});
            var Q7;
            {var subQ2=sQuery(id+"F15.wireOp",EDGE,"E76.6");Q7=makeQuery(id+"F15.imprint","IMPRINT",FACE,{"disambiguationData":[TD([[makeQuery(id+"F15.imprint","IMPRINT",EDGE,{"derivedFrom":subQ2}),-1.0]])]});}
            var Q8;
            Q8=makeQuery(id+"F15.imprint","IMPRINT",FACE,{"disambiguationData":[TD([[makeQuery(id+"F15.imprint","IMPRINT",EDGE,{"derivedFrom":sQuery(id+"F15.wireOp",EDGE,"E78.bottom")}),1.0]])]});
            var Q9;
            Q9=makeQuery(id+"F15.imprint","IMPRINT",FACE,{"disambiguationData":[TD([[makeQuery(id+"F15.imprint","IMPRINT",EDGE,{"derivedFrom":sQuery(id+"F15.wireOp",EDGE,"E79.bottom")}),-1.0]])]});
            extrude(context, id + "F16", {"entities" : qUnion([Q0, Q1, Q2, Q3, Q4, Q5, Q6, Q7, Q8, Q9]), "depth" : 10 * mm, "offsetDistance" : 25 * mm});
        }
        {
            var Q0;
            Q0=makeQuery(id+"F16.opExtrude","CAP_FACE",FACE,{"disambiguationData":[OSD([sQuery(id+"F15.wireOp",EDGE,"E76.13"),sQuery(id+"F15.wireOp",EDGE,"E76.14"),sQuery(id+"F15.wireOp",EDGE,"E77.bottom"),sQuery(id+"F15.wireOp",EDGE,"E77.top"),sQuery(id+"F15.wireOp",EDGE,"E76.5"),sQuery(id+"F15.wireOp",EDGE,"E76.2")])],"isStart":true});
            var sketch = newSketch(context, id + "F17", { "sketchPlane" : qUnion([Q0])});
            skPoint(sketch, "E80.2", {"position": v(22.23, 25.1) * mm});
            skPoint(sketch, "E80.3", {"position": v(22.23, 19.5) * mm});
            skLineSegment(sketch, "E80.6", {"start": v(22.23, 19.5) * mm, "end": v(22.23, 25.1) * mm});
            skLineSegment(sketch, "E80.7", {"start": v(22.23, 19.5) * mm, "end": v(24.23, 19.5) * mm});
            skLineSegment(sketch, "E80.8", {"start": v(24.23, 15) * mm, "end": v(24.23, 19.5) * mm});
            skLineSegment(sketch, "E81.bottom", {"start": v(24.23, 15) * mm, "end": v(16.13, 15) * mm});
            skLineSegment(sketch, "E81.top", {"start": v(24.23, 19.5) * mm, "end": v(16.13, 19.5) * mm});
            skLineSegment(sketch, "E81.right", {"start": v(16.13, 15) * mm, "end": v(16.13, 19.5) * mm});
            skLineSegment(sketch, "E82.bottom", {"start": v(22.23, 19.5) * mm, "end": v(16.13, 19.5) * mm});
            skLineSegment(sketch, "E82.top", {"start": v(22.23, 25.1) * mm, "end": v(16.13, 25.1) * mm});
            skLineSegment(sketch, "E82.right", {"start": v(16.13, 19.5) * mm, "end": v(16.13, 25.1) * mm});
            skLineSegment(sketch, "E83.bottom", {"start": v(16.13, 25.1) * mm, "end": v(24.23, 25.1) * mm});
            skLineSegment(sketch, "E83.top", {"start": v(16.13, 30.3) * mm, "end": v(24.23, 30.3) * mm});
            skLineSegment(sketch, "E83.left", {"start": v(16.13, 25.1) * mm, "end": v(16.13, 30.3) * mm});
            skLineSegment(sketch, "E83.right", {"start": v(24.23, 25.1) * mm, "end": v(24.23, 30.3) * mm});
            skSolve(sketch);
        }
        {
            var Q0;
            Q0 = qSketchRegion(id + "F17", true);
            var Q1;
            Q1=sQuery(id+"F17.wireOp",EDGE,"E82.right");
            revolve(context, id + "F18", {"operationType" : NewBodyOperationType.REMOVE, "entities" : qUnion([Q0]), "axis" : qUnion([Q1]), "revolveType" : RevolveType.FULL, "oppositeDirection" : true});
        }
        {
            var Q0;
            Q0=makeQuery(id+"F16.opExtrude","CAP_FACE",FACE,{"disambiguationData":[OSD([sQuery(id+"F15.wireOp",EDGE,"E76.13"),sQuery(id+"F15.wireOp",EDGE,"E76.14"),sQuery(id+"F15.wireOp",EDGE,"E77.bottom"),sQuery(id+"F15.wireOp",EDGE,"E77.top"),sQuery(id+"F15.wireOp",EDGE,"E76.5"),sQuery(id+"F15.wireOp",EDGE,"E76.2")])],"isStart":false});
            var sketch = newSketch(context, id + "F19", { "sketchPlane" : qUnion([Q0])});
            skCircle(sketch, "E84.0", {"center": v(7.01, -22.3) * mm, "radius": 1.4 * mm});
            skCircle(sketch, "E84.1", {"center": v(25.24, -22.3) * mm, "radius": 1.4 * mm});
            skCircle(sketch, "E85", {"center": v(7.01, -22.3) * mm, "radius": 3.4 * mm});
            skCircle(sketch, "E86", {"center": v(25.24, -22.3) * mm, "radius": 3.4 * mm});
            skSolve(sketch);
        }
        {
            var Q0;
            Q0=makeQuery(id+"F19.imprint","IMPRINT",FACE,{"disambiguationData":[TD([[makeQuery(id+"F19.imprint","IMPRINT",EDGE,{"derivedFrom":sQuery(id+"F19.wireOp",EDGE,"E84.0")}),-1.0]])]});
            var Q1;
            Q1=makeQuery(id+"F19.imprint","IMPRINT",FACE,{"disambiguationData":[TD([[makeQuery(id+"F19.imprint","IMPRINT",EDGE,{"derivedFrom":sQuery(id+"F19.wireOp",EDGE,"E84.1")}),-1.0]])]});
            extrude(context, id + "F20", {"entities" : qUnion([Q0, Q1]), "operationType" : NewBodyOperationType.REMOVE, "oppositeDirection" : true, "depth" : 2 * mm, "offsetDistance" : 25 * mm});
        }
        {
            var Q0;
            Q0=makeQuery(id+"F1.opExtrude","CAP_FACE",FACE,{"disambiguationData":[OSD([sQuery(id+"F0.wireOp",EDGE,"E0.bottom"),sQuery(id+"F0.wireOp",EDGE,"E0.top"),sQuery(id+"F0.wireOp",EDGE,"E0.left"),sQuery(id+"F0.wireOp",EDGE,"E0.right"),sQuery(id+"F0.wireOp",EDGE,"E1.top"),sQuery(id+"F0.wireOp",EDGE,"E1.left"),sQuery(id+"F0.wireOp",EDGE,"E1.right"),sQuery(id+"F0.wireOp",EDGE,"E2.bottom"),sQuery(id+"F0.wireOp",EDGE,"E2.top"),sQuery(id+"F0.wireOp",EDGE,"E2.right"),sQuery(id+"F0.wireOp",EDGE,"E3"),sQuery(id+"F0.wireOp",EDGE,"E5.MirrorC"),sQuery(id+"F0.wireOp",EDGE,"E6"),sQuery(id+"F0.wireOp",EDGE,"E7.MirrorC"),sQuery(id+"F0.wireOp",EDGE,"E8"),sQuery(id+"F0.wireOp",EDGE,"E9.MirrorC"),sQuery(id+"F0.wireOp",EDGE,"E10"),sQuery(id+"F0.wireOp",EDGE,"E11.MirrorC"),sQuery(id+"F0.wireOp",EDGE,"E12"),sQuery(id+"F0.wireOp",EDGE,"E14.MirrorC"),sQuery(id+"F0.wireOp",EDGE,"E16"),sQuery(id+"F0.wireOp",EDGE,"E17"),sQuery(id+"F0.wireOp",EDGE,"E18.MirrorC"),sQuery(id+"F0.wireOp",EDGE,"E19.MirrorC"),sQuery(id+"F0.wireOp",EDGE,"E20"),sQuery(id+"F0.wireOp",EDGE,"E25.MirrorC"),sQuery(id+"F0.wireOp",EDGE,"E26.MirrorC"),sQuery(id+"F0.wireOp",EDGE,"a45dcdff-8f47-47a6-94de-daccb21566b90.MirrorC"),sQuery(id+"F0.wireOp",EDGE,"c506a873-8e33-4dee-948d-999e04e901bd0.MirrorC"),sQuery(id+"F0.wireOp",EDGE,"0d328794-d52e-4739-910c-511e7e9b0b190.MirrorC"),sQuery(id+"F0.wireOp",EDGE,"E27"),sQuery(id+"F0.wireOp",EDGE,"E28"),sQuery(id+"F0.wireOp",EDGE,"E29"),sQuery(id+"F0.wireOp",EDGE,"E31"),sQuery(id+"F0.wireOp",EDGE,"E32.MirrorC"),sQuery(id+"F0.wireOp",EDGE,"E33")])],"isStart":false});
            var sketch = newSketch(context, id + "F21", { "sketchPlane" : qUnion([Q0])});
            skCircle(sketch, "E87.0", {"center": v(39.5, -43) * mm, "radius": 1.5 * mm});
            skCircle(sketch, "E87.1", {"center": v(49, -43) * mm, "radius": 1.5 * mm});
            skLineSegment(sketch, "E88.bottom", {"start": v(34.5, -38) * mm, "end": v(54, -38) * mm});
            skLineSegment(sketch, "E88.top", {"start": v(34.5, -50) * mm, "end": v(54, -50) * mm});
            skLineSegment(sketch, "E88.left", {"start": v(34.5, -38) * mm, "end": v(34.5, -50) * mm});
            skLineSegment(sketch, "E88.right", {"start": v(54, -38) * mm, "end": v(54, -50) * mm});
            skSolve(sketch);
        }
        {
            var Q0;
            Q0=makeQuery(id+"F21.imprint","IMPRINT",FACE,{"disambiguationData":[TD([[makeQuery(id+"F21.imprint","IMPRINT",EDGE,{"derivedFrom":sQuery(id+"F21.wireOp",EDGE,"E87.0")}),-1.0]])]});
            extrude(context, id + "F22", {"entities" : qUnion([Q0]), "depth" : 4 * mm, "offsetDistance" : 25 * mm});
        }
        {
            var Q0;
            Q0=makeQuery(id+"F22.opExtrude","CAP_FACE",FACE,{"disambiguationData":[OSD([sQuery(id+"F21.wireOp",EDGE,"E87.0"),sQuery(id+"F21.wireOp",EDGE,"E87.1"),sQuery(id+"F21.wireOp",EDGE,"E88.bottom"),sQuery(id+"F21.wireOp",EDGE,"E88.top"),sQuery(id+"F21.wireOp",EDGE,"E88.left"),sQuery(id+"F21.wireOp",EDGE,"E88.right")])],"isStart":false});
            var sketch = newSketch(context, id + "F23", { "sketchPlane" : qUnion([Q0])});
            skCircle(sketch, "E89.0", {"center": v(39.5, -43) * mm, "radius": 1.5 * mm});
            skCircle(sketch, "E89.1", {"center": v(49, -43) * mm, "radius": 1.5 * mm});
            skCircle(sketch, "E90", {"center": v(39.5, -43) * mm, "radius": 3.4 * mm});
            skCircle(sketch, "E91", {"center": v(49, -43) * mm, "radius": 3.4 * mm});
            skSolve(sketch);
        }
        {
            var Q0;
            Q0=makeQuery(id+"F23.imprint","IMPRINT",FACE,{"disambiguationData":[TD([[makeQuery(id+"F23.imprint","IMPRINT",EDGE,{"derivedFrom":sQuery(id+"F23.wireOp",EDGE,"E89.0")}),-1.0]])]});
            var Q1;
            Q1=makeQuery(id+"F23.imprint","IMPRINT",FACE,{"disambiguationData":[TD([[makeQuery(id+"F23.imprint","IMPRINT",EDGE,{"derivedFrom":sQuery(id+"F23.wireOp",EDGE,"E89.1")}),-1.0]])]});
            extrude(context, id + "F24", {"entities" : qUnion([Q0, Q1]), "operationType" : NewBodyOperationType.REMOVE, "oppositeDirection" : true, "depth" : 1 * mm, "offsetDistance" : 25 * mm});
        }
        {
            var Q0;
            Q0=makeQuery(id+"F22.opExtrude","CAP_FACE",FACE,{"disambiguationData":[OSD([sQuery(id+"F21.wireOp",EDGE,"E87.0"),sQuery(id+"F21.wireOp",EDGE,"E87.1"),sQuery(id+"F21.wireOp",EDGE,"E88.bottom"),sQuery(id+"F21.wireOp",EDGE,"E88.top"),sQuery(id+"F21.wireOp",EDGE,"E88.left"),sQuery(id+"F21.wireOp",EDGE,"E88.right")])],"isStart":false});
            var sketch = newSketch(context, id + "F25", { "sketchPlane" : qUnion([Q0])});
            skLineSegment(sketch, "E92.bottom", {"start": v(34.5, -47) * mm, "end": v(54, -47) * mm});
            skLineSegment(sketch, "E92.top", {"start": v(34.5, -49) * mm, "end": v(54, -49) * mm});
            skLineSegment(sketch, "E92.left", {"start": v(34.5, -47) * mm, "end": v(34.5, -49) * mm});
            skLineSegment(sketch, "E92.right", {"start": v(54, -47) * mm, "end": v(54, -49) * mm});
            skSolve(sketch);
        }
        {
            var Q0;
            Q0=makeQuery(id+"F25.imprint","IMPRINT",FACE,{"disambiguationData":[TD([[makeQuery(id+"F25.imprint","IMPRINT",EDGE,{"derivedFrom":sQuery(id+"F25.wireOp",EDGE,"E92.bottom")}),-1.0]])]});
            extrude(context, id + "F26", {"entities" : qUnion([Q0]), "operationType" : NewBodyOperationType.ADD, "depth" : 10 * mm, "offsetDistance" : 25 * mm});
        }
        {
            var Q0;
            Q0=makeQuery(id+"F26.opExtrude","SWEPT_FACE",FACE,{"disambiguationData":[OSD([sQuery(id+"F25.wireOp",EDGE,"E92.bottom")])]});
            var sketch = newSketch(context, id + "F27", { "sketchPlane" : qUnion([Q0])});
            skLineSegment(sketch, "E93.0", {"start": v(-34.5, 8) * mm, "end": v(-54, 8) * mm});
            skLineSegment(sketch, "E93.1", {"start": v(-34.5, 18) * mm, "end": v(-34.5, 8) * mm});
            skLineSegment(sketch, "E93.2", {"start": v(-54, 18) * mm, "end": v(-54, 8) * mm});
            skLineSegment(sketch, "E94.0", {"start": v(-34.5, 18) * mm, "end": v(-54, 18) * mm});
            skArc(sketch, "E95", {"start": v(-34.5, 18) * mm, "mid": v(-44.25, 27.75) * mm, "end": v(-54, 18) * mm});
            skSolve(sketch);
        }
        {
            var Q0;
            Q0=makeQuery(id+"F27.imprint","IMPRINT",FACE,{"disambiguationData":[TD([[makeQuery(id+"F27.imprint","IMPRINT",EDGE,{"derivedFrom":sQuery(id+"F27.wireOp",EDGE,"E94.0")}),-1.0]])]});
            extrude(context, id + "F28", {"entities" : qUnion([Q0]), "operationType" : NewBodyOperationType.ADD, "oppositeDirection" : true, "depth" : 2 * mm, "offsetDistance" : 25 * mm});
        }
        {
            var Q0;
            Q0=makeQuery(id+"F28.boolean.opBoolean","MERGE",FACE,{"derivedFrom":[makeQuery(id+"F26.opExtrude","SWEPT_FACE",FACE,{"disambiguationData":[OSD([sQuery(id+"F25.wireOp",EDGE,"E92.bottom")])]}),makeQuery(id+"F28.opExtrude","CAP_FACE",FACE,{"disambiguationData":[OSD([sQuery(id+"F27.wireOp",EDGE,"E94.0"),sQuery(id+"F27.wireOp",EDGE,"E95")])],"isStart":true})]});
            var sketch = newSketch(context, id + "F29", { "sketchPlane" : qUnion([Q0])});
            skLineSegment(sketch, "E96.0", {"start": v(-34.5, 18) * mm, "end": v(-34.5, 8) * mm});
            skLineSegment(sketch, "E96.1", {"start": v(-34.5, 8) * mm, "end": v(-54, 8) * mm});
            skLineSegment(sketch, "E96.2", {"start": v(-54, 18) * mm, "end": v(-54, 8) * mm});
            skLineSegment(sketch, "E97", {"start": v(-34.5, 18) * mm, "end": v(-54, 18) * mm, "construction": true});
            skCircle(sketch, "E98", {"center": v(-44.25, 18) * mm, "radius": 6.75 * mm});
            skSolve(sketch);
        }
        {
            var Q0;
            Q0=makeQuery(id+"F29.imprint","IMPRINT",FACE,{"disambiguationData":[TD([[makeQuery(id+"F29.imprint","IMPRINT",EDGE,{"derivedFrom":sQuery(id+"F29.wireOp",EDGE,"E98")}),1.0]])]});
            extrude(context, id + "F30", {"entities" : qUnion([Q0]), "operationType" : NewBodyOperationType.REMOVE, "endBound" : BoundingType.UP_TO_NEXT, "oppositeDirection" : true, "depth" : 25 * mm, "offsetDistance" : 25 * mm});
        }
        {
            var Q0;
            Q0=makeQuery(id+"F26.boolean.opBoolean","MERGE",FACE,{"derivedFrom":[makeQuery(id+"F22.opExtrude","SWEPT_FACE",FACE,{"disambiguationData":[OSD([sQuery(id+"F21.wireOp",EDGE,"E88.right")])]}),makeQuery(id+"F26.opExtrude","SWEPT_FACE",FACE,{"disambiguationData":[OSD([sQuery(id+"F25.wireOp",EDGE,"E92.right")])]})]});
            var sketch = newSketch(context, id + "F31", { "sketchPlane" : qUnion([Q0])});
            skLineSegment(sketch, "E99.0", {"start": v(-50, 8) * mm, "end": v(-50, 4) * mm});
            skLineSegment(sketch, "E99.1", {"start": v(-49, 8) * mm, "end": v(-50, 8) * mm});
            skLineSegment(sketch, "E99.2", {"start": v(-49, 18) * mm, "end": v(-49, 8) * mm});
            skLineSegment(sketch, "E100", {"start": v(-50, 8) * mm, "end": v(-49, 9.73) * mm});
            skSolve(sketch);
        }
        {
            var Q0;
            {var subQ0=sQuery(id+"F31.wireOp",EDGE,"E99.1");Q0=makeQuery(id+"F31.imprint","IMPRINT",FACE,{"disambiguationData":[TD([[makeQuery(id+"F31.imprint","IMPRINT",EDGE,{"derivedFrom":subQ0}),-1.0]])]});}
            extrude(context, id + "F32", {"entities" : qUnion([Q0]), "operationType" : NewBodyOperationType.ADD, "oppositeDirection" : true, "depth" : 19.5 * mm, "offsetDistance" : 25 * mm});
        }
        {
            var Q0;
            Q0=makeQuery(id+"F32.boolean.opBoolean","MERGE",EDGE,{"derivedFrom":[makeQuery(id+"F22.opExtrude","CAP_EDGE",EDGE,{"disambiguationData":[OSD([sQuery(id+"F21.wireOp",EDGE,"E88.top")])],"isStart":false}),makeQuery(id+"F32.opExtrude","SWEPT_EDGE",EDGE,{"disambiguationData":[OSD([sQuery(id+"F31.wireOp",EDGE,"E99.0"),sQuery(id+"F31.wireOp",EDGE,"E99.1"),sQuery(id+"F31.wireOp",EDGE,"E100")])]})]});
            var Q1;
            Q1=makeQuery(id+"F32.opExtrude","SWEPT_EDGE",EDGE,{"disambiguationData":[OSD([sQuery(id+"F31.wireOp",EDGE,"E99.2"),sQuery(id+"F31.wireOp",EDGE,"E100")])]});
            fillet(context, id + "F33", {"entities" : qUnion([Q0, Q1]), "radius" : 1 * mm, "tangentPropagation" : true, "allowEdgeOverflow" : false});
        }
        {
            var Q0;
            Q0=makeQuery(id+"F6.opExtrude","CAP_EDGE",EDGE,{"disambiguationData":[OSD([sQuery(id+"F4.wireOp",EDGE,"E54.4")])],"isStart":false});
            var Q1;
            Q1=makeQuery(id+"F6.opExtrude","CAP_EDGE",EDGE,{"disambiguationData":[OSD([sQuery(id+"F4.wireOp",EDGE,"E54.5"),sQuery(id+"F4.wireOp",EDGE,"E55")])],"isStart":false});
            var Q2;
            Q2=makeQuery(id+"F6.opExtrude","CAP_EDGE",EDGE,{"disambiguationData":[OSD([sQuery(id+"F4.wireOp",EDGE,"E54.1")])],"isStart":false});
            fillet(context, id + "F34", {"entities" : qUnion([Q0, Q1, Q2]), "radius" : 1 * mm, "tangentPropagation" : true, "allowEdgeOverflow" : false});
        }
        {
            var Q0;
            Q0=makeQuery(id+"F16.opExtrude","SWEPT_FACE",FACE,{"disambiguationData":[OSD([sQuery(id+"F15.wireOp",EDGE,"E79.right")])]});
            var sketch = newSketch(context, id + "F35", { "sketchPlane" : qUnion([Q0])});
            skLineSegment(sketch, "E101.0", {"start": v(-15, 28) * mm, "end": v(-15, 18) * mm});
            skLineSegment(sketch, "E101.1", {"start": v(-15, 18) * mm, "end": v(-30.3, 18) * mm});
            skLineSegment(sketch, "E101.2", {"start": v(-15, 28) * mm, "end": v(-30.3, 28) * mm});
            skLineSegment(sketch, "E101.3", {"start": v(-30.3, 28) * mm, "end": v(-30.3, 18) * mm});
            skSolve(sketch);
        }
        {
            var Q0;
            Q0=makeQuery(id+"F35.imprint","IMPRINT",FACE,{"disambiguationData":[TD([[makeQuery(id+"F35.imprint","IMPRINT",EDGE,{"derivedFrom":sQuery(id+"F35.wireOp",EDGE,"E101.2")}),1.0]])]});
            extrude(context, id + "F36", {"entities" : qUnion([Q0]), "operationType" : NewBodyOperationType.ADD, "depth" : 4 * mm, "offsetDistance" : 25 * mm});
        }
        {
            var Q0;
            Q0=makeQuery(id+"F16.opExtrude","CAP_FACE",FACE,{"disambiguationData":[OSD([sQuery(id+"F15.wireOp",EDGE,"E76.13"),sQuery(id+"F15.wireOp",EDGE,"E76.14"),sQuery(id+"F15.wireOp",EDGE,"E77.bottom"),sQuery(id+"F15.wireOp",EDGE,"E77.top"),sQuery(id+"F15.wireOp",EDGE,"E78.bottom"),sQuery(id+"F15.wireOp",EDGE,"E78.top"),sQuery(id+"F15.wireOp",EDGE,"E78.right"),sQuery(id+"F15.wireOp",EDGE,"E79.bottom"),sQuery(id+"F15.wireOp",EDGE,"E79.top"),sQuery(id+"F15.wireOp",EDGE,"E79.right")])],"isStart":false});
            var sketch = newSketch(context, id + "F37", { "sketchPlane" : qUnion([Q0])});
            skLineSegment(sketch, "E102.0", {"start": v(0, -15) * mm, "end": v(32.25, -15) * mm});
            skLineSegment(sketch, "E102.1", {"start": v(0, -15) * mm, "end": v(0, -30.3) * mm});
            skLineSegment(sketch, "E102.2", {"start": v(0, -30.3) * mm, "end": v(32.25, -30.3) * mm});
            skLineSegment(sketch, "E103", {"start": v(18.13, -15) * mm, "end": v(18.13, -30.3) * mm, "construction": true});
            skLineSegment(sketch, "E104.bottom", {"start": v(12.13, -15) * mm, "end": v(18.13, -15) * mm});
            skLineSegment(sketch, "E104.top", {"start": v(12.13, -30.3) * mm, "end": v(18.13, -30.3) * mm});
            skLineSegment(sketch, "E104.left", {"start": v(12.13, -15) * mm, "end": v(12.13, -30.3) * mm});
            skLineSegment(sketch, "E104.right", {"start": v(18.13, -15) * mm, "end": v(18.13, -30.3) * mm});
            skLineSegment(sketch, "E105.0", {"start": v(0, -15) * mm, "end": v(36.25, -15) * mm});
            skLineSegment(sketch, "E105.1", {"start": v(0, -30.3) * mm, "end": v(36.25, -30.3) * mm});
            skLineSegment(sketch, "E105.2", {"start": v(36.25, -15) * mm, "end": v(36.25, -30.3) * mm});
            skLineSegment(sketch, "E106.bottom", {"start": v(36.25, -15) * mm, "end": v(30.25, -15) * mm});
            skLineSegment(sketch, "E106.top", {"start": v(36.25, -30.3) * mm, "end": v(30.25, -30.3) * mm});
            skLineSegment(sketch, "E106.right", {"start": v(30.25, -15) * mm, "end": v(30.25, -30.3) * mm});
            skSolve(sketch);
        }
        {
            var Q0;
            Q0=makeQuery(id+"F37.imprint","IMPRINT",FACE,{"disambiguationData":[TD([[makeQuery(id+"F37.imprint","IMPRINT",EDGE,{"derivedFrom":sQuery(id+"F37.wireOp",EDGE,"E104.bottom")}),-1.0]])]});
            var Q1;
            {var subQ0=sQuery(id+"F37.wireOp",EDGE,"E105.2");Q1=makeQuery(id+"F37.imprint","IMPRINT",FACE,{"disambiguationData":[TD([[makeQuery(id+"F37.imprint","IMPRINT",EDGE,{"derivedFrom":subQ0}),-1.0]])]});}
            var Q2;
            {var subQ8=sQuery(id+"F37.wireOp",EDGE,"E104.left");Q2=makeQuery(id+"F37.imprint","IMPRINT",FACE,{"disambiguationData":[TD([[makeQuery(id+"F37.imprint","IMPRINT",EDGE,{"derivedFrom":subQ8}),1.0]])]});}
            extrude(context, id + "F38", {"entities" : qUnion([Q0, Q1, Q2]), "operationType" : NewBodyOperationType.ADD, "depth" : 6 * mm, "offsetDistance" : 25 * mm});
        }
        {
            var Q0;
            Q0=makeQuery(id+"F3.opExtrude","SWEPT_BODY",BODY,{"disambiguationData":[OSD([sQuery(id+"F2.wireOp",EDGE,"E39.9"),sQuery(id+"F2.wireOp",EDGE,"E39.10"),sQuery(id+"F2.wireOp",EDGE,"E39.11"),sQuery(id+"F2.wireOp",EDGE,"E45"),sQuery(id+"F2.wireOp",EDGE,"E46"),sQuery(id+"F2.wireOp",EDGE,"E47"),sQuery(id+"F2.wireOp",EDGE,"E48"),sQuery(id+"F2.wireOp",EDGE,"E49"),sQuery(id+"F2.wireOp",EDGE,"E50"),sQuery(id+"F2.wireOp",EDGE,"E51")])]});
            deleteBodies(context, id + "F39", {"entities" : qUnion([Q0])});
        }
        {
            var Q0;
            Q0=makeQuery(id+"F38.boolean.opBoolean","MERGE",FACE,{"derivedFrom":[makeQuery(id+"F36.opExtrude","CAP_FACE",FACE,{"disambiguationData":[OSD([sQuery(id+"F35.wireOp",EDGE,"E101.2"),sQuery(id+"F35.wireOp",EDGE,"E101.1"),sQuery(id+"F35.wireOp",EDGE,"E101.0"),sQuery(id+"F35.wireOp",EDGE,"E101.3")])],"isStart":false}),makeQuery(id+"F38.opExtrude","SWEPT_FACE",FACE,{"disambiguationData":[OSD([sQuery(id+"F37.wireOp",EDGE,"E105.2")])]})]});
            var sketch = newSketch(context, id + "F40", { "sketchPlane" : qUnion([Q0])});
            skLineSegment(sketch, "E107.1", {"start": v(-15, 34) * mm, "end": v(-30.3, 34) * mm});
            skLineSegment(sketch, "E107.3", {"start": v(-15, 18) * mm, "end": v(-30.3, 18) * mm});
            skLineSegment(sketch, "E108.top", {"start": v(-15, 30) * mm, "end": v(-30.3, 30) * mm});
            skLineSegment(sketch, "E108.left", {"start": v(-15, 34) * mm, "end": v(-15, 30) * mm});
            skLineSegment(sketch, "E108.right", {"start": v(-30.3, 34) * mm, "end": v(-30.3, 30) * mm});
            skSolve(sketch);
        }
        {
            var Q0;
            Q0=makeQuery(id+"F40.imprint","IMPRINT",FACE,{"disambiguationData":[TD([[makeQuery(id+"F40.imprint","IMPRINT",EDGE,{"derivedFrom":sQuery(id+"F40.wireOp",EDGE,"E107.1")}),1.0]])]});
            extrude(context, id + "F41", {"entities" : qUnion([Q0]), "operationType" : NewBodyOperationType.ADD, "depth" : 19 * mm, "offsetDistance" : 25 * mm});
        }
        {
            var Q0;
            Q0=makeQuery(id+"F41.boolean.opBoolean","MERGE",FACE,{"derivedFrom":[makeQuery(id+"F38.opExtrude","CAP_FACE",FACE,{"disambiguationData":[OSD([sQuery(id+"F37.wireOp",EDGE,"E106.bottom"),sQuery(id+"F37.wireOp",EDGE,"E106.top"),sQuery(id+"F37.wireOp",EDGE,"E105.2"),sQuery(id+"F37.wireOp",EDGE,"E106.right")])],"isStart":false}),makeQuery(id+"F41.opExtrude","SWEPT_FACE",FACE,{"disambiguationData":[OSD([sQuery(id+"F40.wireOp",EDGE,"E107.1")])]})]});
            var sketch = newSketch(context, id + "F42", { "sketchPlane" : qUnion([Q0])});
            skLineSegment(sketch, "E109.0", {"start": v(12.13, -15) * mm, "end": v(18.13, -15) * mm});
            skLineSegment(sketch, "E109.1", {"start": v(12.13, -15) * mm, "end": v(12.13, -30.3) * mm});
            skLineSegment(sketch, "E109.2", {"start": v(18.13, -15) * mm, "end": v(18.13, -30.3) * mm});
            skLineSegment(sketch, "E109.3", {"start": v(12.13, -30.3) * mm, "end": v(18.13, -30.3) * mm});
            skLineSegment(sketch, "E109.4", {"start": v(30.25, -30.3) * mm, "end": v(55.25, -30.3) * mm});
            skLineSegment(sketch, "E109.5", {"start": v(30.25, -15) * mm, "end": v(30.25, -30.3) * mm});
            skLineSegment(sketch, "E109.6", {"start": v(30.25, -15) * mm, "end": v(55.25, -15) * mm});
            skLineSegment(sketch, "E109.7", {"start": v(55.25, -15) * mm, "end": v(55.25, -30.3) * mm});
            skLineSegment(sketch, "E110", {"start": v(15.13, -15) * mm, "end": v(15.13, -30.3) * mm, "construction": true});
            skCircle(sketch, "E111", {"center": v(15.13, -24.3) * mm, "radius": 1.4 * mm});
            skCircle(sketch, "E112", {"center": v(50.33, -24.3) * mm, "radius": 1.5 * mm});
            skSolve(sketch);
        }
        {
            var Q0;
            Q0=makeQuery(id+"F42.imprint","IMPRINT",FACE,{"disambiguationData":[TD([[makeQuery(id+"F42.imprint","IMPRINT",EDGE,{"derivedFrom":sQuery(id+"F42.wireOp",EDGE,"E111")}),1.0]])]});
            var Q1;
            Q1=makeQuery(id+"F42.imprint","IMPRINT",FACE,{"disambiguationData":[TD([[makeQuery(id+"F42.imprint","IMPRINT",EDGE,{"derivedFrom":sQuery(id+"F42.wireOp",EDGE,"E112")}),1.0]])]});
            extrude(context, id + "F43", {"entities" : qUnion([Q0, Q1]), "operationType" : NewBodyOperationType.REMOVE, "oppositeDirection" : true, "depth" : 20 * mm, "offsetDistance" : 25 * mm});
        }
    });
